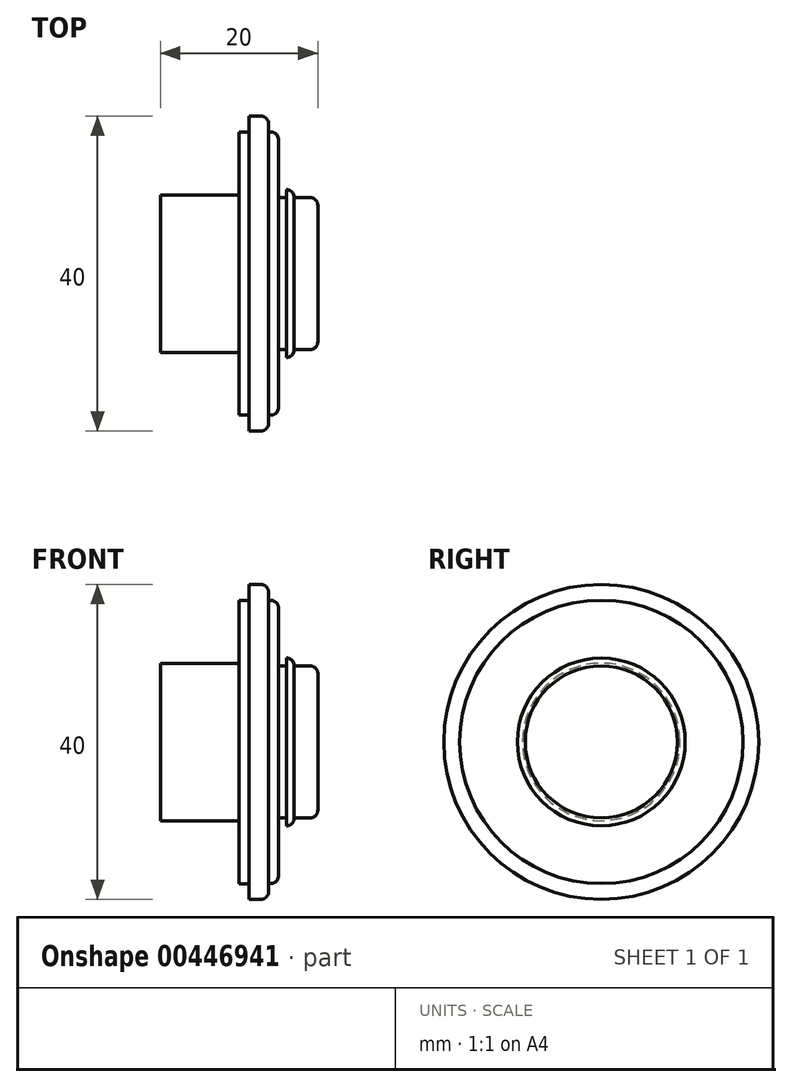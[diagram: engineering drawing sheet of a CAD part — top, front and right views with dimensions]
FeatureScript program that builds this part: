
annotation { "Feature Type Name" : "Feature", "Feature Type Description" : "" }
export const myFeature = defineFeature(function(context is Context, id is Id, definition is map)
    precondition{}
    {
        {
            var Q0;
            Q0=qCreatedBy(makeId("Front.planeOp"),FACE);
            var sketch = newSketch(context, id + "F0", { "sketchPlane" : qUnion([Q0])});
            skLineSegment(sketch, "E0", {"start": v(0, 0) * mm, "end": v(0, 10) * mm});
            skLineSegment(sketch, "E1", {"start": v(0, 10) * mm, "end": v(10, 10) * mm});
            skLineSegment(sketch, "E2", {"start": v(10, 10) * mm, "end": v(10, 18) * mm});
            skLineSegment(sketch, "E3", {"start": v(11.25, 18) * mm, "end": v(11.25, 20) * mm});
            skLineSegment(sketch, "E4", {"start": v(11.25, 20) * mm, "end": v(13.75, 20) * mm});
            skLineSegment(sketch, "E5", {"start": v(13.75, 20) * mm, "end": v(13.75, 18) * mm});
            skLineSegment(sketch, "E6", {"start": v(13.75, 18) * mm, "end": v(15, 18) * mm});
            skLineSegment(sketch, "E7", {"start": v(15, 18) * mm, "end": v(15, 9.66) * mm});
            skLineSegment(sketch, "E8", {"start": v(15, 9.66) * mm, "end": v(16, 9.66) * mm});
            skLineSegment(sketch, "E9", {"start": v(16, 9.66) * mm, "end": v(16, 10.66) * mm});
            skLineSegment(sketch, "E10", {"start": v(16, 10.66) * mm, "end": v(17, 10.66) * mm});
            skLineSegment(sketch, "E11", {"start": v(17, 10.66) * mm, "end": v(17, 9.66) * mm});
            skLineSegment(sketch, "E12", {"start": v(17, 9.66) * mm, "end": v(20, 9.66) * mm});
            skLineSegment(sketch, "E13", {"start": v(20, 9.66) * mm, "end": v(20, 0) * mm});
            skLineSegment(sketch, "E14", {"start": v(20, 0) * mm, "end": v(0, 0) * mm});
            skLineSegment(sketch, "E15", {"start": v(10, 18) * mm, "end": v(11.25, 18) * mm});
            skSolve(sketch);
        }
        {
            var Q0;
            Q0 = qSketchRegion(id + "F0", true);
            var Q1;
            Q1=sQuery(id+"F0.wireOp",EDGE,"E14");
            revolve(context, id + "F1", {"entities" : qUnion([Q0]), "axis" : qUnion([Q1]), "revolveType" : RevolveType.FULL});
        }
        {
            var Q0;
            Q0=makeQuery(id+"F1.opRevolve","SWEPT_EDGE",EDGE,{"disambiguationData":[OSD([sQuery(id+"F0.wireOp",EDGE,"E12"),sQuery(id+"F0.wireOp",EDGE,"E13")])]});
            var Q1;
            Q1=makeQuery(id+"F1.opRevolve","SWEPT_EDGE",EDGE,{"disambiguationData":[OSD([sQuery(id+"F0.wireOp",EDGE,"E10"),sQuery(id+"F0.wireOp",EDGE,"E11")])]});
            var Q2;
            Q2=makeQuery(id+"F1.opRevolve","SWEPT_EDGE",EDGE,{"disambiguationData":[OSD([sQuery(id+"F0.wireOp",EDGE,"E6"),sQuery(id+"F0.wireOp",EDGE,"E7")])]});
            var Q3;
            Q3=makeQuery(id+"F1.opRevolve","SWEPT_EDGE",EDGE,{"disambiguationData":[OSD([sQuery(id+"F0.wireOp",EDGE,"E4"),sQuery(id+"F0.wireOp",EDGE,"E5")])]});
            fillet(context, id + "F2", {"entities" : qUnion([Q0, Q1, Q2, Q3]), "radius" : 1 * mm, "tangentPropagation" : true, "allowEdgeOverflow" : false});
        }
    });
